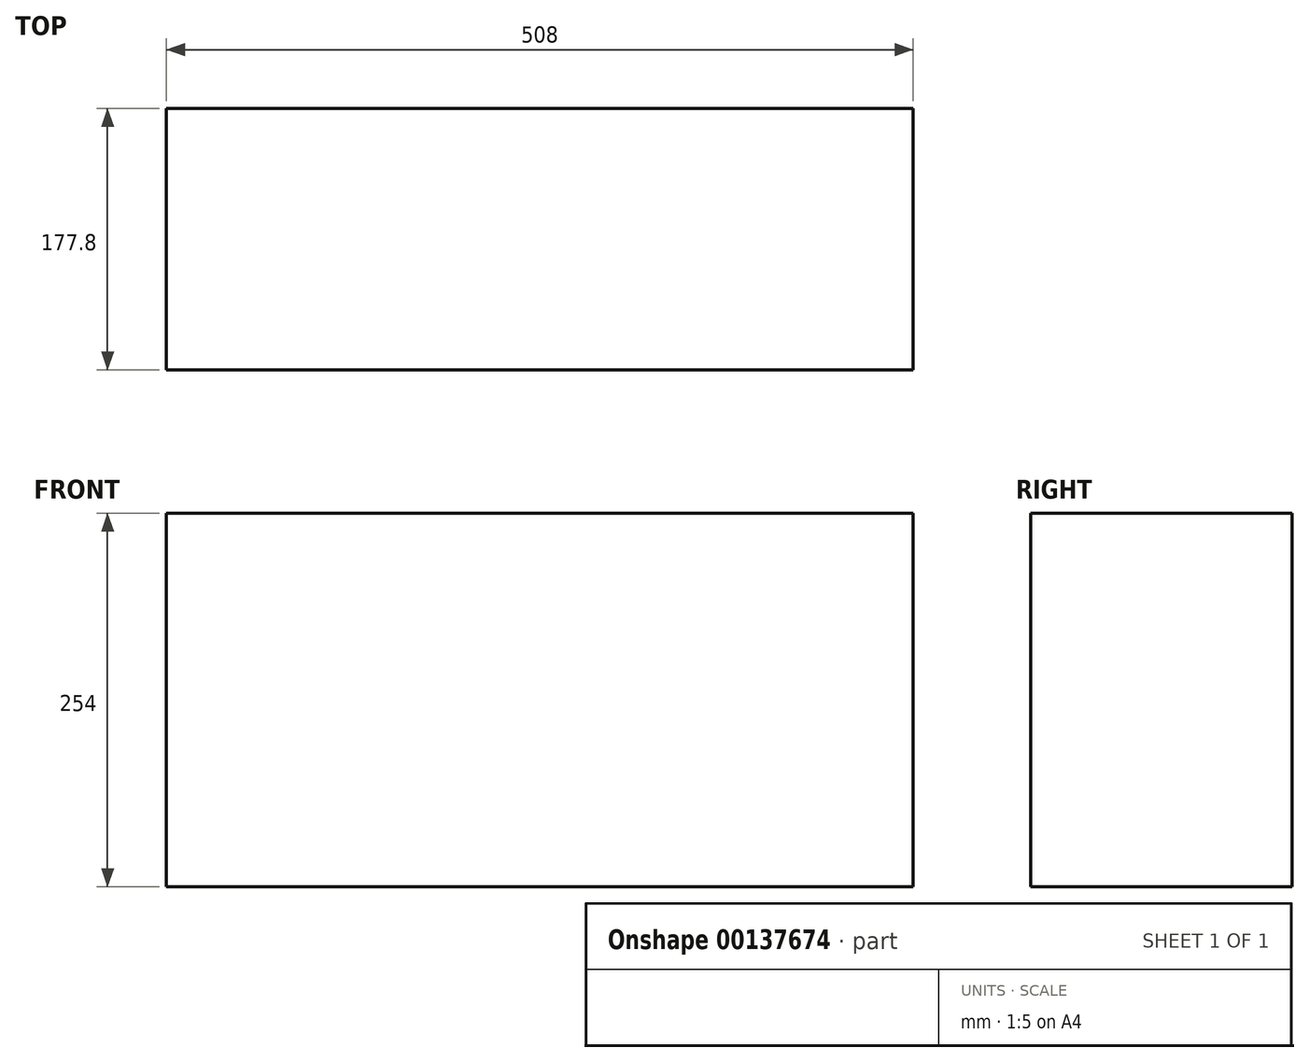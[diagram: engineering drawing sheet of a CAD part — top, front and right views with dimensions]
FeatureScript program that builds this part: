
annotation { "Feature Type Name" : "Feature", "Feature Type Description" : "" }
export const myFeature = defineFeature(function(context is Context, id is Id, definition is map)
    precondition{}
    {
        {
            var Q0;
            Q0=qCreatedBy(makeId("Front.planeOp"),FACE);
            var sketch = newSketch(context, id + "F0", { "sketchPlane" : qUnion([Q0])});
            skLineSegment(sketch, "E0.bottom", {"start": v(0, 0) * mm, "end": v(508, 0) * mm});
            skLineSegment(sketch, "E0.top", {"start": v(0, 254) * mm, "end": v(508, 254) * mm});
            skLineSegment(sketch, "E0.left", {"start": v(0, 0) * mm, "end": v(0, 254) * mm});
            skLineSegment(sketch, "E0.right", {"start": v(508, 0) * mm, "end": v(508, 254) * mm});
            skSolve(sketch);
        }
        {
            var Q0;
            Q0=makeQuery(id+"F0.imprint","IMPRINT",FACE,{"disambiguationData":[TD([[makeQuery(id+"F0.imprint","IMPRINT",EDGE,{"derivedFrom":sQuery(id+"F0.wireOp",EDGE,"E0.bottom")}),1.0]])]});
            extrude(context, id + "F1", {"entities" : qUnion([Q0]), "depth" : 177.8 * mm});
        }
    });
